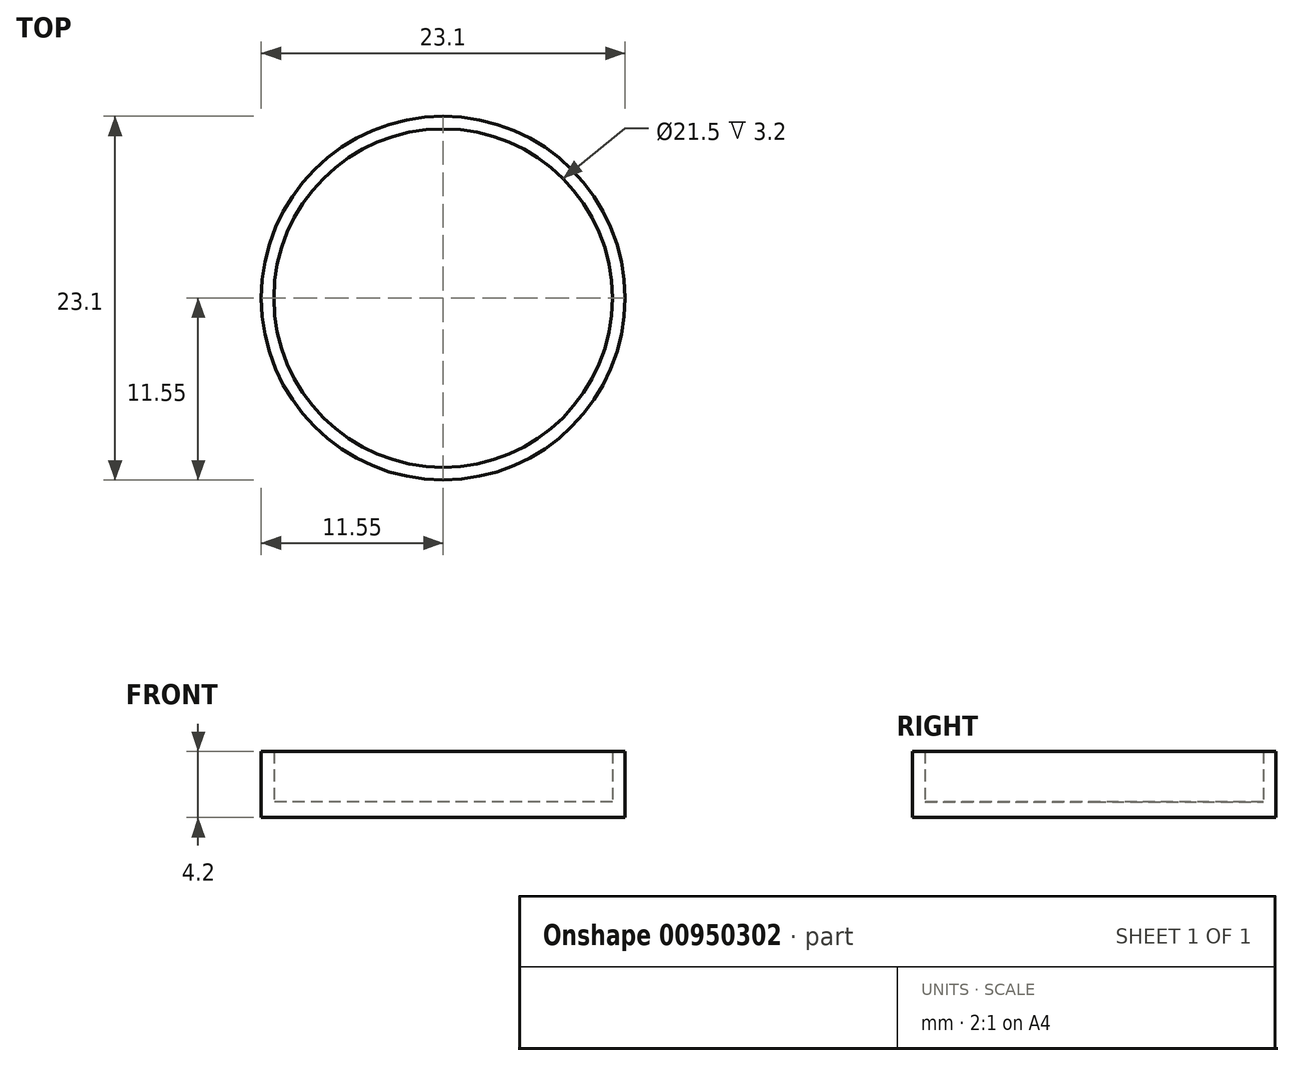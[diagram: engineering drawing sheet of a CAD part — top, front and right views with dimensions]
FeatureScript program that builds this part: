
annotation { "Feature Type Name" : "Feature", "Feature Type Description" : "" }
export const myFeature = defineFeature(function(context is Context, id is Id, definition is map)
    precondition{}
    {
        {
            var Q0;
            Q0=qCreatedBy(makeId("Top.planeOp"),FACE);
            var sketch = newSketch(context, id + "F0", { "sketchPlane" : qUnion([Q0])});
            skCircle(sketch, "E0", {"center": v(0, 0) * mm, "radius": 10.75 * mm});
            skCircle(sketch, "E1", {"center": v(0, 0) * mm, "radius": 11.55 * mm});
            skSolve(sketch);
        }
        {
            var Q0;
            Q0 = qSketchRegion(id + "F0", true);
            extrude(context, id + "F1", {"entities" : qUnion([Q0]), "depth" : 3.2 * mm, "offsetDistance" : 25 * mm});
        }
        {
            var Q0;
            Q0=makeQuery(id+"F0.imprint","IMPRINT",FACE,{"disambiguationData":[TD([[makeQuery(id+"F0.imprint","IMPRINT",EDGE,{"derivedFrom":sQuery(id+"F0.wireOp",EDGE,"E0")}),1.0]])]});
            var Q1;
            Q1=makeQuery(id+"F0.imprint","IMPRINT",FACE,{"disambiguationData":[TD([[makeQuery(id+"F0.imprint","IMPRINT",EDGE,{"derivedFrom":sQuery(id+"F0.wireOp",EDGE,"E0")}),-1.0]])]});
            extrude(context, id + "F2", {"entities" : qUnion([Q0, Q1]), "operationType" : NewBodyOperationType.ADD, "oppositeDirection" : true, "depth" : 1 * mm, "offsetDistance" : 25 * mm});
        }
    });
